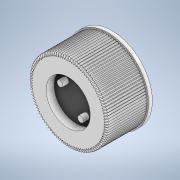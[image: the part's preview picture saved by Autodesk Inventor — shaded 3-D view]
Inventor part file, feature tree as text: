
AUTODESK INVENTOR PART (.ipt)
format: ipt  version: 2021 (Build 250183000, 183)  size: 806,912 bytes
history: native  units: mm
features: sketch x5, extrude x4, fillet x1
ambient origin geometry x8: Origin, YZ Plane, XZ Plane, XY Plane, X Axis, Y Axis, Z Axis, Center Point
bodies: Solid1 (feature_tree)
feature tree (10):
  extrude  "Extrusion1"  Depth=1.3mm TaperAngle=0.0deg
  extrude  "Extrusion2"  Depth=25.8mm
  sketch  "Sketch3"  dims[d9=13.5mm d10=0.0mm d11=0.5mm]
  fillet  "Fillet1"  Radius=1000.0mm
  extrude  "Extrusion3"  Depth=0.5mm
  extrude  "Extrusion4"  Depth=2.7mm TaperAngle=0.0deg
  sketch  "Sketch1"  dims[d0=27.6mm d1=1.3mm d2=0.0mm]
  sketch  "Sketch2"  dims[d3=26.8mm d4=25.8mm d5=1000.0mm d7=360.0deg]
  sketch  "Sketch4"  dims[d12=15.0mm d13=2.7mm d14=0.0mm]
  sketch  "Sketch5"  dims[d15=7.0mm d16=7.0mm d17=3.5mm d18=3.5mm d19=2.0mm d20=2.0mm d21=2.0mm d22=0.0mm]
